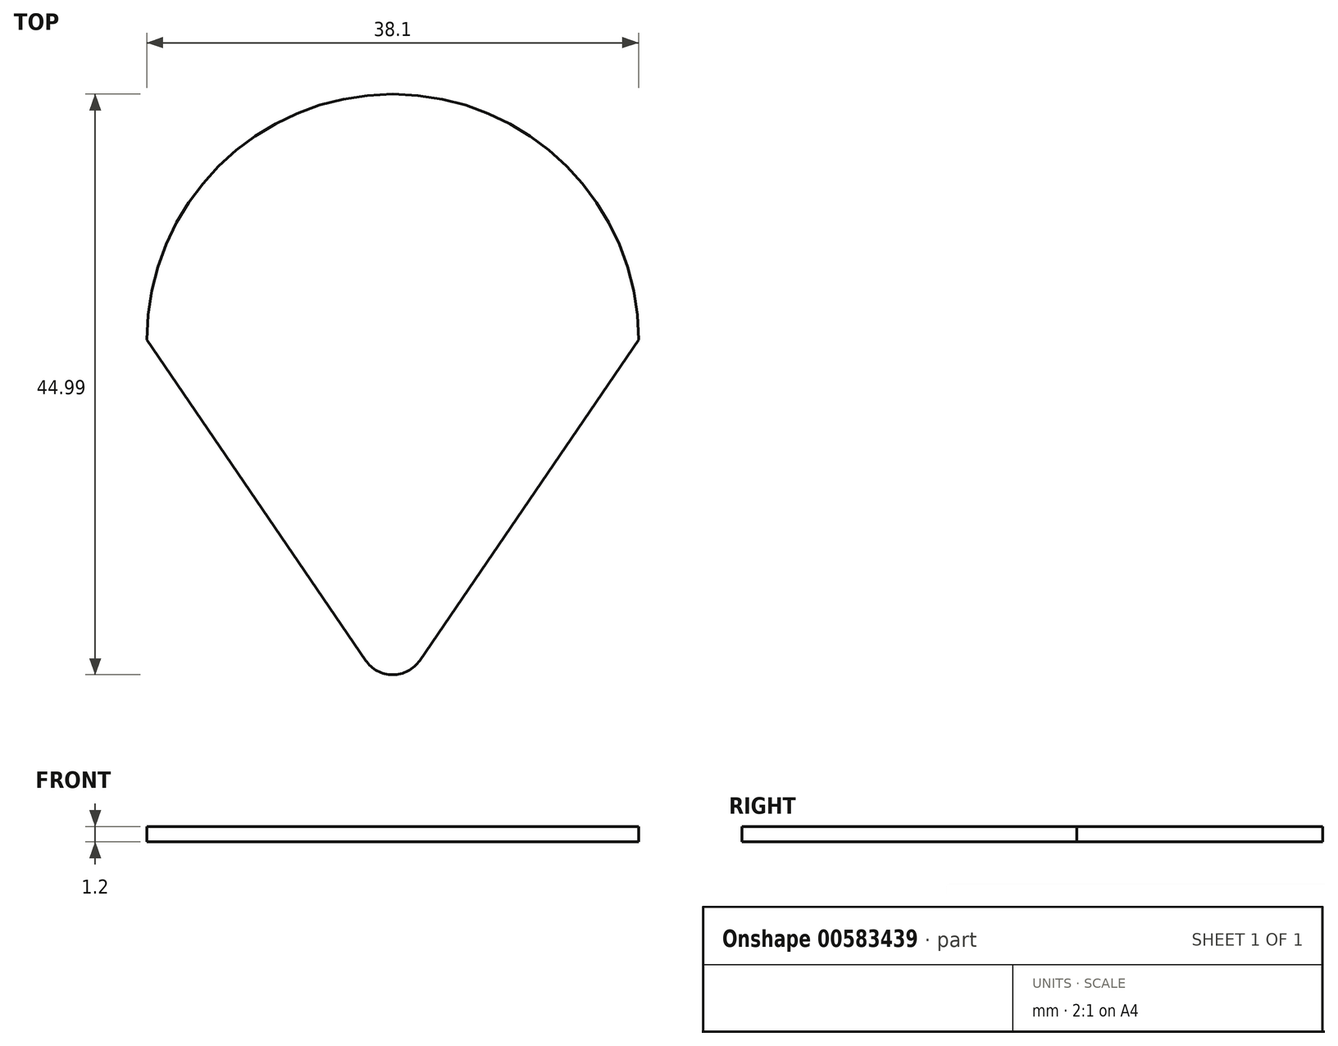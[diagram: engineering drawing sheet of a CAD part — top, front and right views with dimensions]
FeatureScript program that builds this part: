
annotation { "Feature Type Name" : "Feature", "Feature Type Description" : "" }
export const myFeature = defineFeature(function(context is Context, id is Id, definition is map)
    precondition{}
    {
        {
            var Q0;
            Q0=qCreatedBy(makeId("Top.planeOp"),FACE);
            var sketch = newSketch(context, id + "F0", { "sketchPlane" : qUnion([Q0])});
            skArc(sketch, "E0", {"start": v(19.05, 0) * mm, "mid": v(0, 19.05) * mm, "end": v(-19.05, 0) * mm});
            skLineSegment(sketch, "E1", {"start": v(-19.05, 0) * mm, "end": v(-2.1, -24.83) * mm});
            skLineSegment(sketch, "E2", {"start": v(2.1, -24.83) * mm, "end": v(19.05, 0) * mm});
            skPoint(sketch, "E3.visualSharp", {"position": v(0, -27.9) * mm});
            skArc(sketch, "E3.filletArc", {"start": v(-2.1, -24.83) * mm, "mid": v(0, -25.94) * mm, "end": v(2.1, -24.83) * mm});
            skSolve(sketch);
        }
        {
            var Q0;
            Q0=makeQuery(id+"F0.imprint","IMPRINT",FACE,{"disambiguationData":[TD([[makeQuery(id+"F0.imprint","IMPRINT",EDGE,{"derivedFrom":sQuery(id+"F0.wireOp",EDGE,"E0")}),1.0]])]});
            extrude(context, id + "F1", {"entities" : qUnion([Q0]), "depth" : 1.2 * mm, "offsetDistance" : 25.4 * mm});
        }
    });
